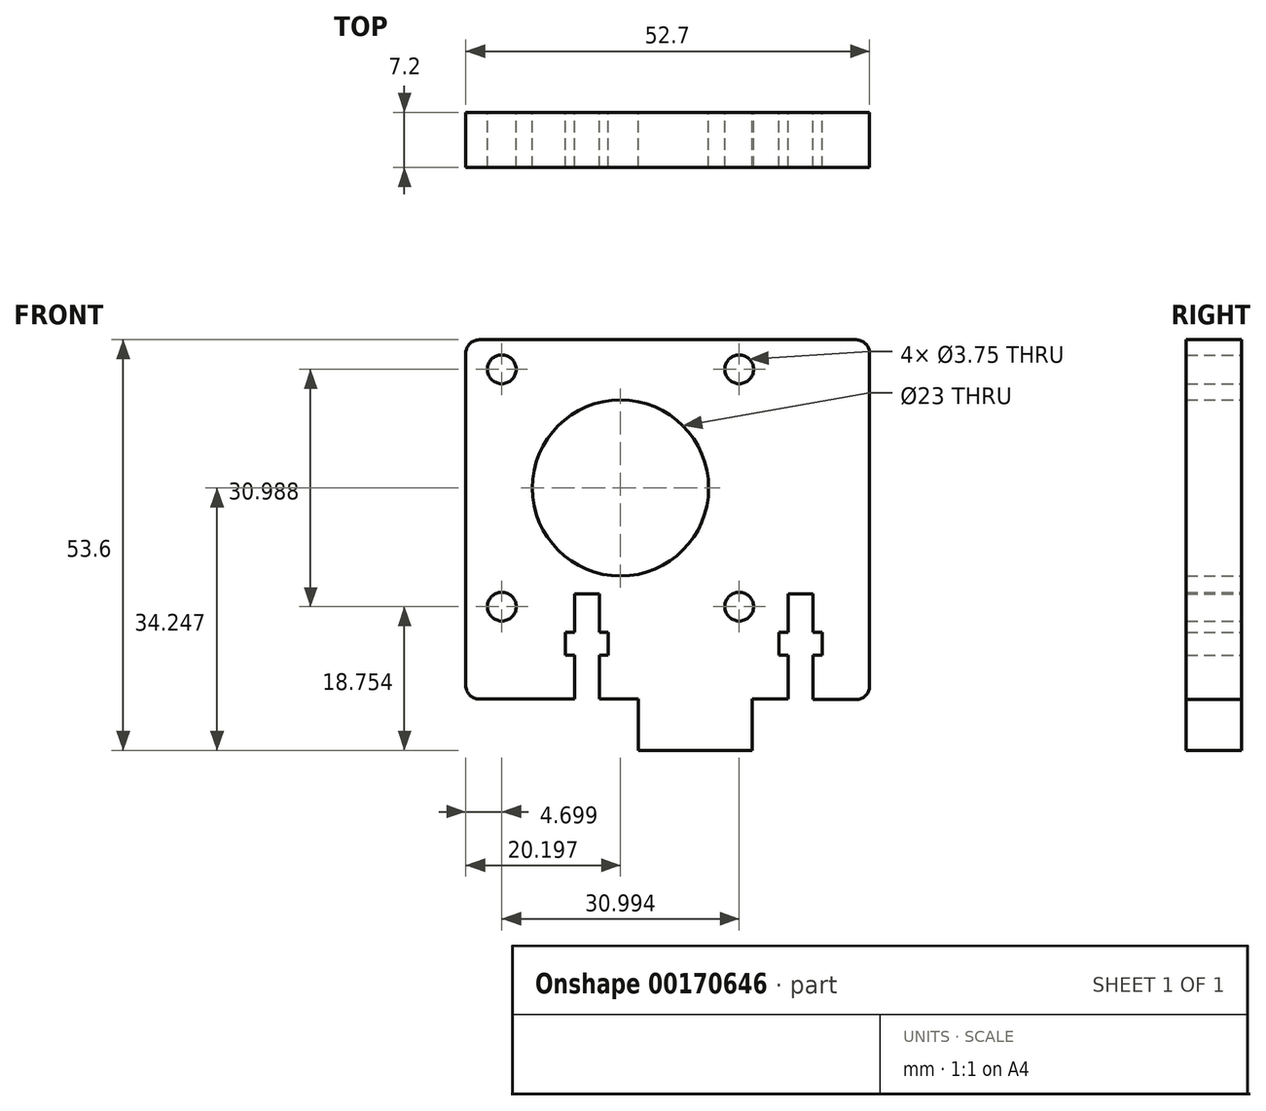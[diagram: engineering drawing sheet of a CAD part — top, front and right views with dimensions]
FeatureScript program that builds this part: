
annotation { "Feature Type Name" : "Feature", "Feature Type Description" : "" }
export const myFeature = defineFeature(function(context is Context, id is Id, definition is map)
    precondition{}
    {
        {
            var Q0;
            Q0=qCreatedBy(makeId("Front.planeOp"),FACE);
            var sketch = newSketch(context, id + "F0", { "sketchPlane" : qUnion([Q0])});
            skLineSegment(sketch, "E0", {"start": v(-39.34, -7.03) * mm, "end": v(-39.34, -18.8) * mm});
            skLineSegment(sketch, "E1", {"start": v(-37.59, -20.54) * mm, "end": v(-25.13, -20.54) * mm});
            skLineSegment(sketch, "E2", {"start": v(-25.13, -20.54) * mm, "end": v(-25.13, -14.84) * mm});
            skLineSegment(sketch, "E3", {"start": v(-25.13, -14.84) * mm, "end": v(-26.33, -14.84) * mm});
            skLineSegment(sketch, "E4", {"start": v(-26.33, -14.84) * mm, "end": v(-26.33, -11.84) * mm});
            skLineSegment(sketch, "E5", {"start": v(-26.33, -11.84) * mm, "end": v(-25.13, -11.84) * mm});
            skLineSegment(sketch, "E6", {"start": v(-25.13, -11.84) * mm, "end": v(-25.13, -6.84) * mm});
            skLineSegment(sketch, "E7", {"start": v(-25.13, -6.84) * mm, "end": v(-21.93, -6.84) * mm});
            skLineSegment(sketch, "E8", {"start": v(-21.93, -6.84) * mm, "end": v(-21.93, -11.84) * mm});
            skLineSegment(sketch, "E9", {"start": v(-21.93, -11.84) * mm, "end": v(-20.73, -11.84) * mm});
            skLineSegment(sketch, "E10", {"start": v(-20.73, -11.84) * mm, "end": v(-20.73, -14.84) * mm});
            skLineSegment(sketch, "E11", {"start": v(-20.73, -14.84) * mm, "end": v(-21.93, -14.84) * mm});
            skLineSegment(sketch, "E12", {"start": v(-21.93, -14.84) * mm, "end": v(-21.93, -20.54) * mm});
            skLineSegment(sketch, "E13", {"start": v(-21.93, -20.54) * mm, "end": v(-16.83, -20.54) * mm});
            skLineSegment(sketch, "E14", {"start": v(-16.83, -20.54) * mm, "end": v(-16.83, -27.24) * mm});
            skLineSegment(sketch, "E15", {"start": v(-16.83, -27.24) * mm, "end": v(-1.99, -27.24) * mm});
            skLineSegment(sketch, "E16", {"start": v(-1.99, -27.24) * mm, "end": v(-1.99, -20.54) * mm});
            skLineSegment(sketch, "E17", {"start": v(-1.99, -20.54) * mm, "end": v(2.76, -20.54) * mm});
            skLineSegment(sketch, "E18", {"start": v(2.76, -20.54) * mm, "end": v(2.76, -14.84) * mm});
            skLineSegment(sketch, "E19", {"start": v(2.76, -14.84) * mm, "end": v(1.56, -14.84) * mm});
            skLineSegment(sketch, "E20", {"start": v(1.56, -14.84) * mm, "end": v(1.56, -11.84) * mm});
            skLineSegment(sketch, "E21", {"start": v(1.56, -11.84) * mm, "end": v(2.76, -11.84) * mm});
            skLineSegment(sketch, "E22", {"start": v(2.76, -11.84) * mm, "end": v(2.76, -6.84) * mm});
            skLineSegment(sketch, "E23", {"start": v(2.76, -6.84) * mm, "end": v(5.96, -6.84) * mm});
            skLineSegment(sketch, "E24", {"start": v(5.96, -6.84) * mm, "end": v(5.96, -11.84) * mm});
            skLineSegment(sketch, "E25", {"start": v(5.96, -11.84) * mm, "end": v(7.16, -11.84) * mm});
            skLineSegment(sketch, "E26", {"start": v(7.16, -11.84) * mm, "end": v(7.16, -14.84) * mm});
            skLineSegment(sketch, "E27", {"start": v(7.16, -14.84) * mm, "end": v(5.96, -14.84) * mm});
            skLineSegment(sketch, "E28", {"start": v(5.96, -14.84) * mm, "end": v(5.96, -20.62) * mm});
            skLineSegment(sketch, "E29", {"start": v(5.96, -20.62) * mm, "end": v(11.61, -20.62) * mm});
            skPoint(sketch, "E30.visualSharp", {"position": v(-39.34, -20.54) * mm});
            skArc(sketch, "E30.filletArc", {"start": v(-39.34, -18.8) * mm, "mid": v(-38.82, -20.03) * mm, "end": v(-37.59, -20.54) * mm});
            skPoint(sketch, "E31.visualSharp", {"position": v(22.96, 26.36) * mm});
            skPoint(sketch, "E32.visualSharp", {"position": v(-33.04, 26.36) * mm});
            skLineSegment(sketch, "E33", {"start": v(13.36, 24.61) * mm, "end": v(13.36, -18.87) * mm});
            skCircle(sketch, "E34", {"center": v(-34.64, 22.5) * mm, "radius": 1.88 * mm});
            skCircle(sketch, "E35", {"center": v(-3.65, 22.5) * mm, "radius": 1.88 * mm});
            skCircle(sketch, "E36", {"center": v(-3.65, -8.49) * mm, "radius": 1.88 * mm});
            skCircle(sketch, "E37", {"center": v(-34.64, -8.49) * mm, "radius": 1.88 * mm});
            skLineSegment(sketch, "E38", {"start": v(-39.34, -7.03) * mm, "end": v(-39.34, 24.61) * mm});
            skCircle(sketch, "E39", {"center": v(-19.14, 7) * mm, "radius": 11.5 * mm});
            skPoint(sketch, "E40.visualSharp", {"position": v(-39.34, 26.36) * mm});
            skArc(sketch, "E40.filletArc", {"start": v(-37.59, 26.36) * mm, "mid": v(-38.82, 25.85) * mm, "end": v(-39.34, 24.61) * mm});
            skPoint(sketch, "E41.visualSharp", {"position": v(13.36, 26.36) * mm});
            skArc(sketch, "E41.filletArc", {"start": v(13.36, 24.61) * mm, "mid": v(12.85, 25.85) * mm, "end": v(11.61, 26.36) * mm});
            skPoint(sketch, "E42.visualSharp", {"position": v(13.36, -20.62) * mm});
            skArc(sketch, "E42.filletArc", {"start": v(11.61, -20.62) * mm, "mid": v(12.85, -20.1) * mm, "end": v(13.36, -18.87) * mm});
            skPoint(sketch, "E43.end.orphan", {"position": v(-29.51, 26.36) * mm});
            skLineSegment(sketch, "E44", {"start": v(-37.59, 26.36) * mm, "end": v(11.61, 26.36) * mm});
            skSolve(sketch);
        }
        {
            var Q0;
            Q0=makeQuery(id+"F0.imprint","IMPRINT",FACE,{"disambiguationData":[TD([[makeQuery(id+"F0.imprint","IMPRINT",EDGE,{"derivedFrom":sQuery(id+"F0.wireOp",EDGE,"E0")}),1.0]])]});
            extrude(context, id + "F1", {"entities" : qUnion([Q0]), "depth" : 7.2 * mm});
        }
    });
